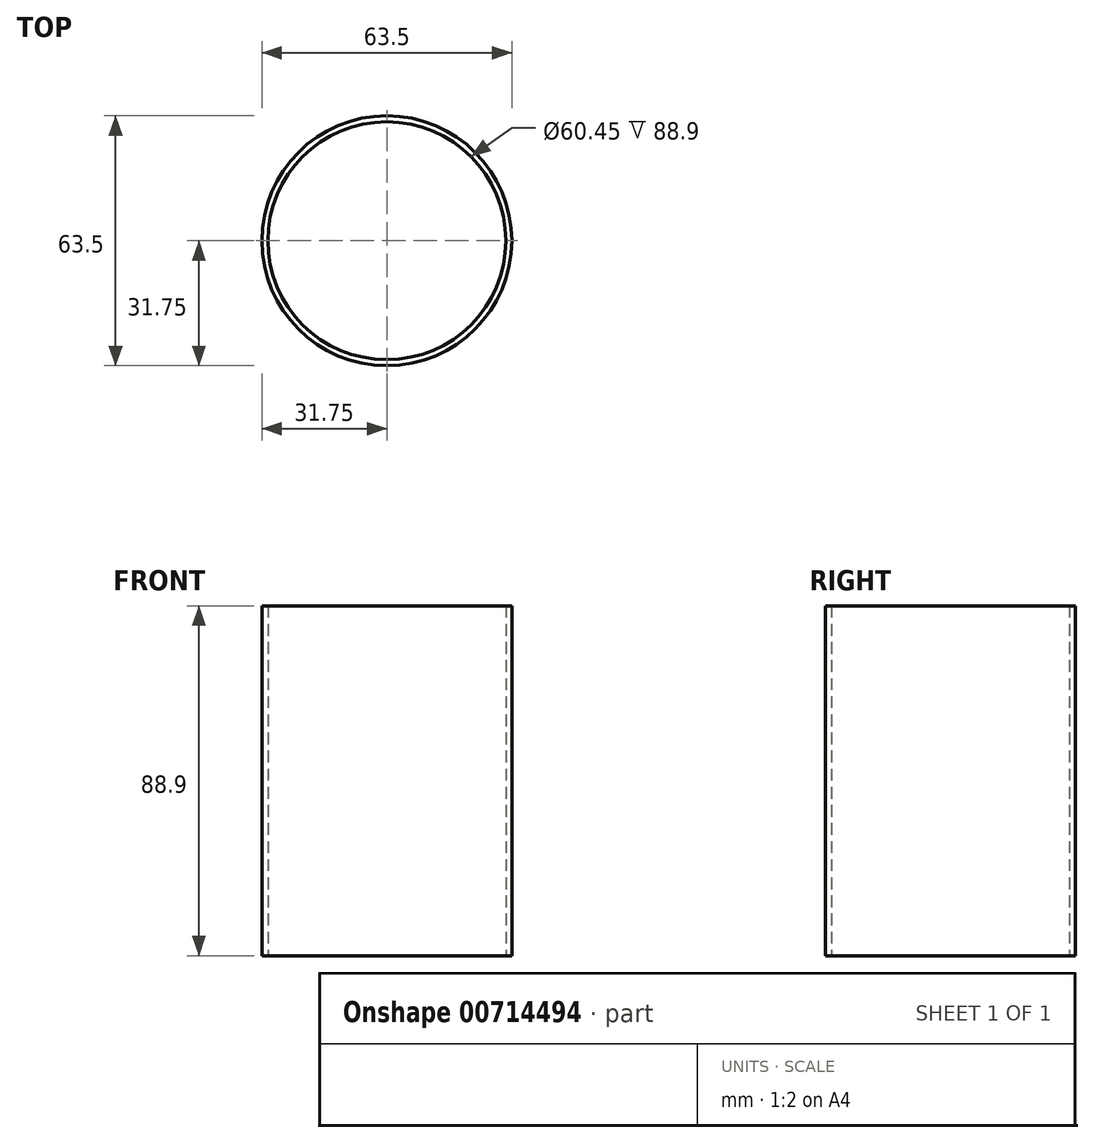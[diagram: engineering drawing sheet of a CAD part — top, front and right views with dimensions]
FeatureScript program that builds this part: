
annotation { "Feature Type Name" : "Feature", "Feature Type Description" : "" }
export const myFeature = defineFeature(function(context is Context, id is Id, definition is map)
    precondition{}
    {
        {
            var Q0;
            Q0=qCreatedBy(makeId("Top.planeOp"),FACE);
            var sketch = newSketch(context, id + "F0", { "sketchPlane" : qUnion([Q0])});
            skCircle(sketch, "E0", {"center": v(0, 0) * mm, "radius": 31.75 * mm});
            skCircle(sketch, "E1.0", {"center": v(0, 0) * mm, "radius": 30.23 * mm});
            skSolve(sketch);
        }
        {
            var Q0;
            Q0 = qSketchRegion(id + "F0", true);
            extrude(context, id + "F1", {"entities" : qUnion([Q0]), "depth" : 88.9 * mm, "offsetDistance" : 25.4 * mm});
        }
    });
